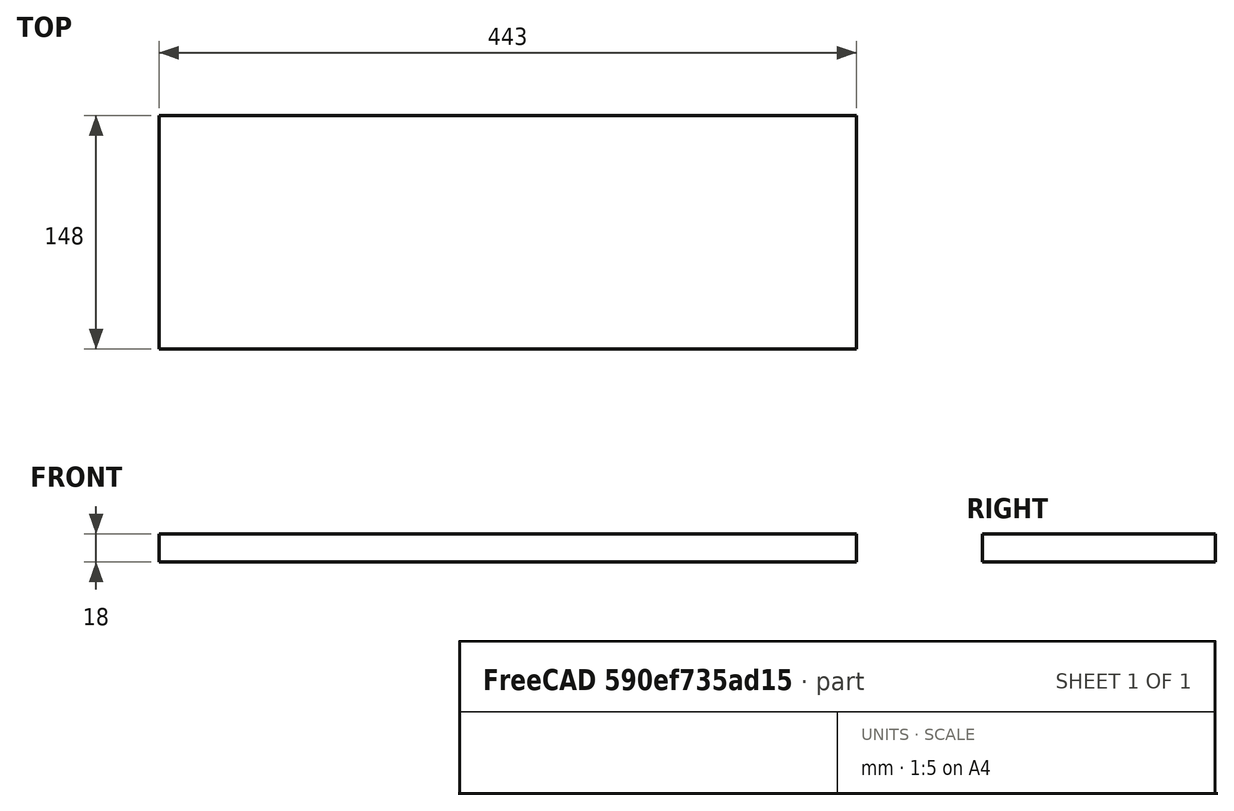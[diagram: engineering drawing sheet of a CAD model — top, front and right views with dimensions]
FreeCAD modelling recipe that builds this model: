
FCSTD DOCUMENT  (FreeCAD 0.17R13541 (Git))
Label: FaceSuperieure
License: All rights reserved
LicenseURL: http://en.wikipedia.org/wiki/All_rights_reserved
objects: Sketcher::SketchObject×1, PartDesign::Pad×1, PartDesign::Body×1
note: 4 computed .brp shape members not serialized (recipe doc carries the construction recipe); baked Part::Feature solids carry a one-line shape summary decoded from their .brp

FEATURE [Sketcher::SketchObject] Sketch
  MapMode = 5
  Support = -> [XY_Plane]
  sketch-geometry (6):
    g0: LineSegment StartX=-221.5 StartY=74 StartZ=0 EndX=221.5 EndY=74 EndZ=0
    g1: LineSegment StartX=221.5 StartY=74 StartZ=0 EndX=221.5 EndY=-74 EndZ=0
    g2: LineSegment StartX=221.5 StartY=-74 StartZ=0 EndX=-221.5 EndY=-74 EndZ=0
    g3: LineSegment StartX=-221.5 StartY=-74 StartZ=0 EndX=-221.5 EndY=74 EndZ=0
    g4: LineSegment [constr] StartX=-221.5 StartY=74 StartZ=0 EndX=221.5 EndY=-74 EndZ=0
    g5: LineSegment [constr] StartX=-221.5 StartY=-74 StartZ=0 EndX=221.5 EndY=74 EndZ=0
  constraints (16):
    c: Coincident(g0,g1)
    c: Coincident(g1,g2)
    c: Coincident(g2,g3)
    c: Coincident(g3,g0)
    c: Horizontal(g0)
    c: Horizontal(g2)
    c: Vertical(g1)
    c: Vertical(g3)
    c: Coincident(g4,g0)
    c: Coincident(g4,g1)
    c: Coincident(g5,g2)
    c: Coincident(g5,g0)
    c: PointOnObject(g-1,g4)
    c: PointOnObject(g-1,g5)
    c: DistanceX(g0,g0) = 443  'Largeur a'
    c: DistanceY(g3,g3) = 148  'Profondeur b'
FEATURE [PartDesign::Pad] Pad
  Length = 18
  Length2 = 100
  Profile = -> Sketch
  Type = 0
FEATURE [PartDesign::Body] Body  label="Face superieure"
  Group = -> [Sketch,Pad]
  Origin = -> Origin
  Tip = -> Pad
